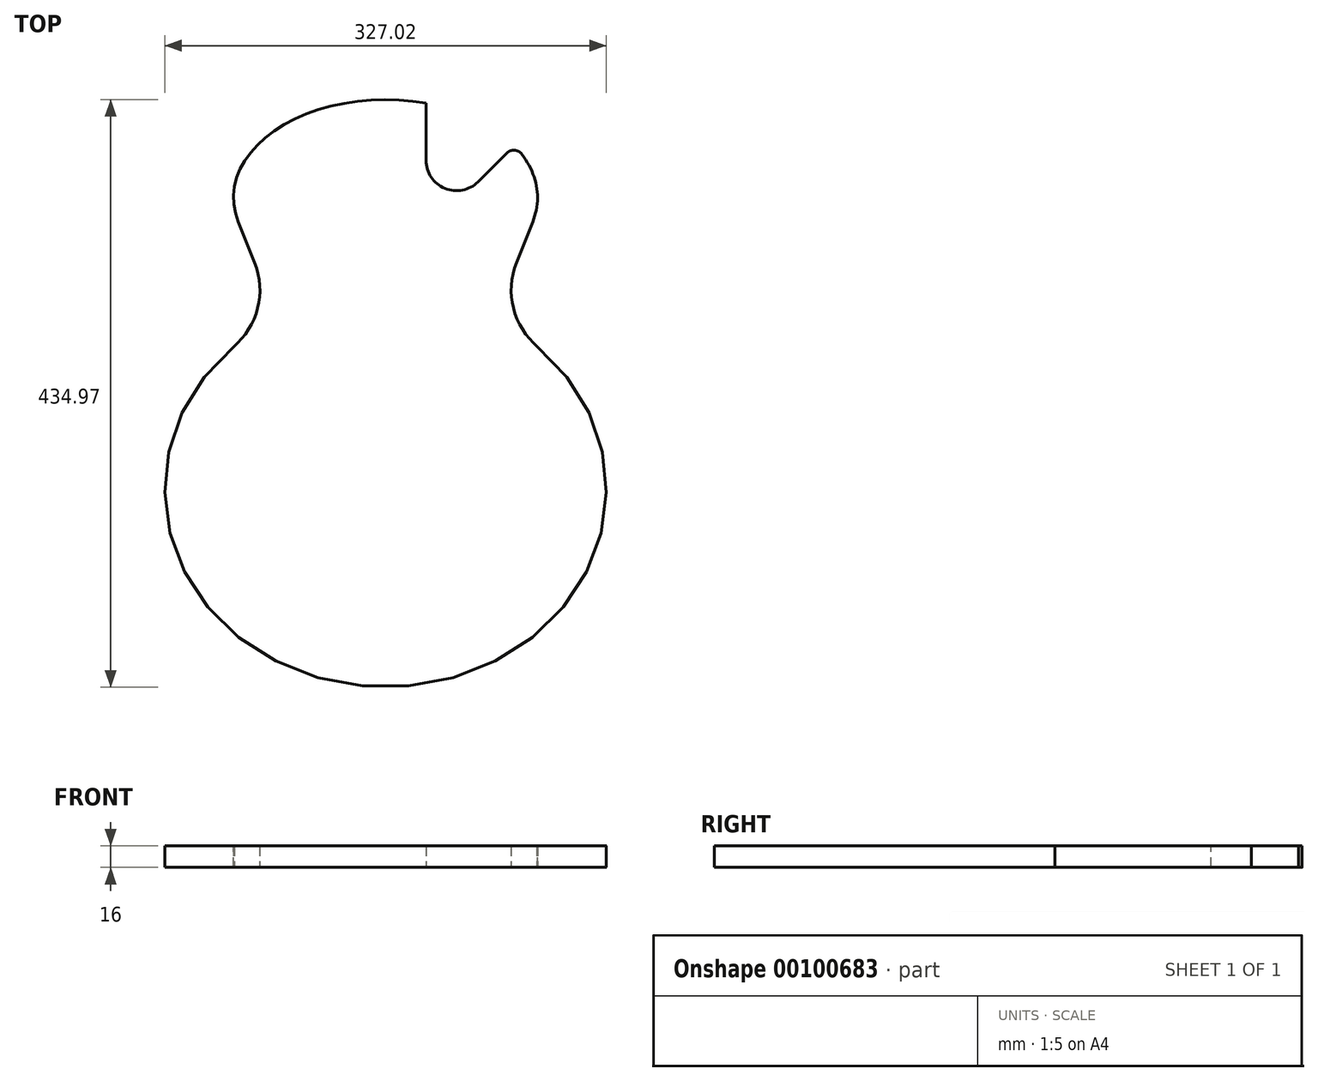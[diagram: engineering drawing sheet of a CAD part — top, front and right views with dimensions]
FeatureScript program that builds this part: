
annotation { "Feature Type Name" : "Feature", "Feature Type Description" : "" }
export const myFeature = defineFeature(function(context is Context, id is Id, definition is map)
    precondition{}
    {
        {
            var Q0;
            Q0=qCreatedBy(makeId("Top.planeOp"),FACE);
            var sketch = newSketch(context, id + "F0", { "sketchPlane" : qUnion([Q0])});
            skEllipticalArc(sketch, "E0", {});
            skEllipticalArc(sketch, "E1", {});
            skLineSegment(sketch, "E2", {"start": v(0, 0) * mm, "end": v(0, 434.98) * mm, "construction": true});
            skLineSegment(sketch, "E3", {"start": v(-244.22, 0) * mm, "end": v(-244.22, 277.4) * mm, "construction": true});
            skLineSegment(sketch, "E4", {"start": v(-244.22, 277.4) * mm, "end": v(0, 277.4) * mm, "construction": true});
            skLineSegment(sketch, "E5", {"start": v(-82.17, 277.4) * mm, "end": v(-111.98, 252.4) * mm, "construction": true});
            skLineSegment(sketch, "E6", {"start": v(-96.94, 314.36) * mm, "end": v(-108.95, 344.4) * mm});
            skArc(sketch, "E7", {"start": v(-112.66, 251.82) * mm, "mid": v(-94.67, 280.54) * mm, "end": v(-96.94, 314.36) * mm});
            skEllipticalArc(sketch, "E8.MirrorCS", {});
            skLineSegment(sketch, "E9.MirrorCS", {"start": v(96.94, 314.36) * mm, "end": v(108.95, 344.4) * mm});
            skArc(sketch, "E10.MirrorCS", {"start": v(112.66, 251.82) * mm, "mid": v(94.67, 280.54) * mm, "end": v(96.94, 314.36) * mm});
            skEllipticalArc(sketch, "E11.MirrorCS", {});
            skPoint(sketch, "E12.orphan", {"position": v(113.61, 356.07) * mm});
            skPoint(sketch, "E13.orphan", {"position": v(-113.61, 356.07) * mm});
            skLineSegment(sketch, "E14", {"start": v(-112.66, 251.82) * mm, "end": v(-111.98, 252.4) * mm});
            skLineSegment(sketch, "E15", {"start": v(111.98, 252.4) * mm, "end": v(112.66, 251.82) * mm});
            const initialGuessF0  = {"E0": [0, 0.146, 0, -1, 0.146, 0.1635125, 3.8959392904465506, 6.283185307179586], "E1": [0, 0.362475, -1, 0, 0.1125, 0.0725, 4.71238898038469, 0.2520546479388711], "E8.MirrorCS": [0, 0.362475, 1, 0, 0.1125, 0.0725, 6.031130659240716, 1.5707963267948966], "E11.MirrorCS": [0, 0.146, 0, -1, 0.146, 0.1635125, 6.283185307179586, 2.387246016733036]};
            skSetInitialGuess(sketch, initialGuessF0);
            skSolve(sketch);
        }
        {
            var Q0;
            Q0=qSketchRegion(id+"F0",true);
            extrude(context, id + "F1", {"entities" : qUnion([Q0]), "depth" : 16 * mm});
        }
        {
            var Q0;
            Q0=makeQuery(id+"F1.opExtrude","CAP_FACE",FACE,{"disambiguationData":[OSD([sQuery(id+"F0.wireOp",EDGE,"E0"),sQuery(id+"F0.wireOp",EDGE,"E1"),sQuery(id+"F0.wireOp",EDGE,"E6"),sQuery(id+"F0.wireOp",EDGE,"E7"),sQuery(id+"F0.wireOp",EDGE,"E8.MirrorCS"),sQuery(id+"F0.wireOp",EDGE,"E9.MirrorCS"),sQuery(id+"F0.wireOp",EDGE,"E10.MirrorCS"),sQuery(id+"F0.wireOp",EDGE,"E11.MirrorCS"),sQuery(id+"F0.wireOp",EDGE,"E14"),sQuery(id+"F0.wireOp",EDGE,"E15")])],"isStart":false});
            var sketch = newSketch(context, id + "F2", { "sketchPlane" : qUnion([Q0])});
            skLineSegment(sketch, "E16", {"start": v(0, 434.98) * mm, "end": v(0, 369.98) * mm, "construction": true});
            skPoint(sketch, "E16.endSnap0", {"position": v(0, 434.98) * mm});
            skLineSegment(sketch, "E17.0", {"start": v(30, 434.98) * mm, "end": v(30, 389.98) * mm});
            skLineSegment(sketch, "E18", {"start": v(0, 434.98) * mm, "end": v(30, 434.98) * mm, "construction": true});
            skArc(sketch, "E19", {"start": v(30, 389.98) * mm, "mid": v(43.89, 369.19) * mm, "end": v(68.4, 374.07) * mm});
            skLineSegment(sketch, "E20", {"start": v(68.4, 374.07) * mm, "end": v(89.64, 395.3) * mm});
            skArc(sketch, "E21", {"start": v(100.9, 394.55) * mm, "mid": v(95.43, 397.47) * mm, "end": v(89.64, 395.3) * mm});
            skLineSegment(sketch, "E22", {"start": v(100.9, 394.55) * mm, "end": v(69.95, 434.98) * mm});
            skLineSegment(sketch, "E23", {"start": v(30, 434.98) * mm, "end": v(69.95, 434.98) * mm});
            skSolve(sketch);
        }
        {
            var Q0;
            Q0=qSketchRegion(id+"F2",true);
            extrude(context, id + "F3", {"entities" : qUnion([Q0]), "operationType" : NewBodyOperationType.REMOVE, "endBound" : BoundingType.THROUGH_ALL, "oppositeDirection" : true, "depth" : 25 * mm});
        }
    });
